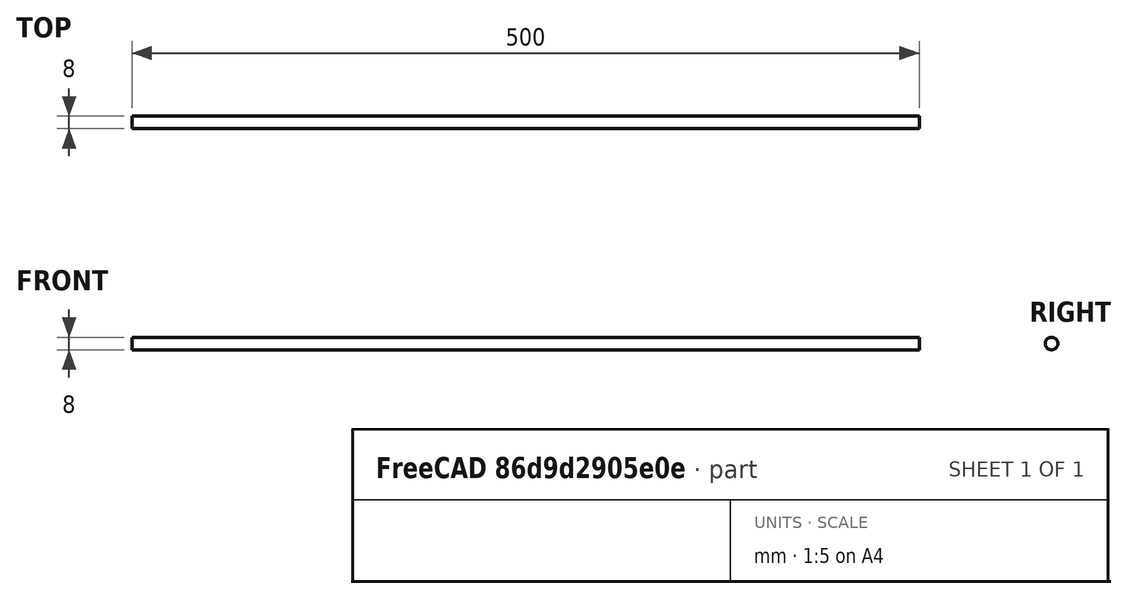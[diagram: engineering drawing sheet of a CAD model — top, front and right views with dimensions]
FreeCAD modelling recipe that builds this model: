
FCSTD DOCUMENT  (FreeCAD 0.19R)
Label: vis_double_8mm_500mm
License: All rights reserved
LicenseURL: http://en.wikipedia.org/wiki/All_rights_reserved
objects: Sketcher::SketchObject×1, PartDesign::Pad×1, PartDesign::Body×1
note: 4 computed .brp shape members not serialized (recipe doc carries the construction recipe); baked Part::Feature solids carry a one-line shape summary decoded from their .brp

FEATURE [Sketcher::SketchObject] Sketch
  FullyConstrained = true
  MapMode = 5
  Placement = pos=(0,0,0) rot=(0.57735,0.57735,0.57735;2.0944rad)
  Support = -> [YZ_Plane]
  sketch-geometry (1):
    g0: Circle CenterX=0 CenterY=0 CenterZ=0 NormalX=0 NormalY=0 NormalZ=1 AngleXU=0 Radius=4
  constraints (2):
    c: Coincident(g0,g-1)
    c: Radius(g0) = 4
FEATURE [PartDesign::Pad] Pad
  Direction = (1,1,1)
  Length = 500
  Length2 = 100
  Midplane = true
  Placement = pos=(0,0,0) rot=(0.57735,0.57735,0.57735;2.0944rad)
  Profile = -> Sketch
  Type = 0
FEATURE [PartDesign::Body] Body
  Group = -> [Sketch,Pad]
  Origin = -> Origin
  Tip = -> Pad
